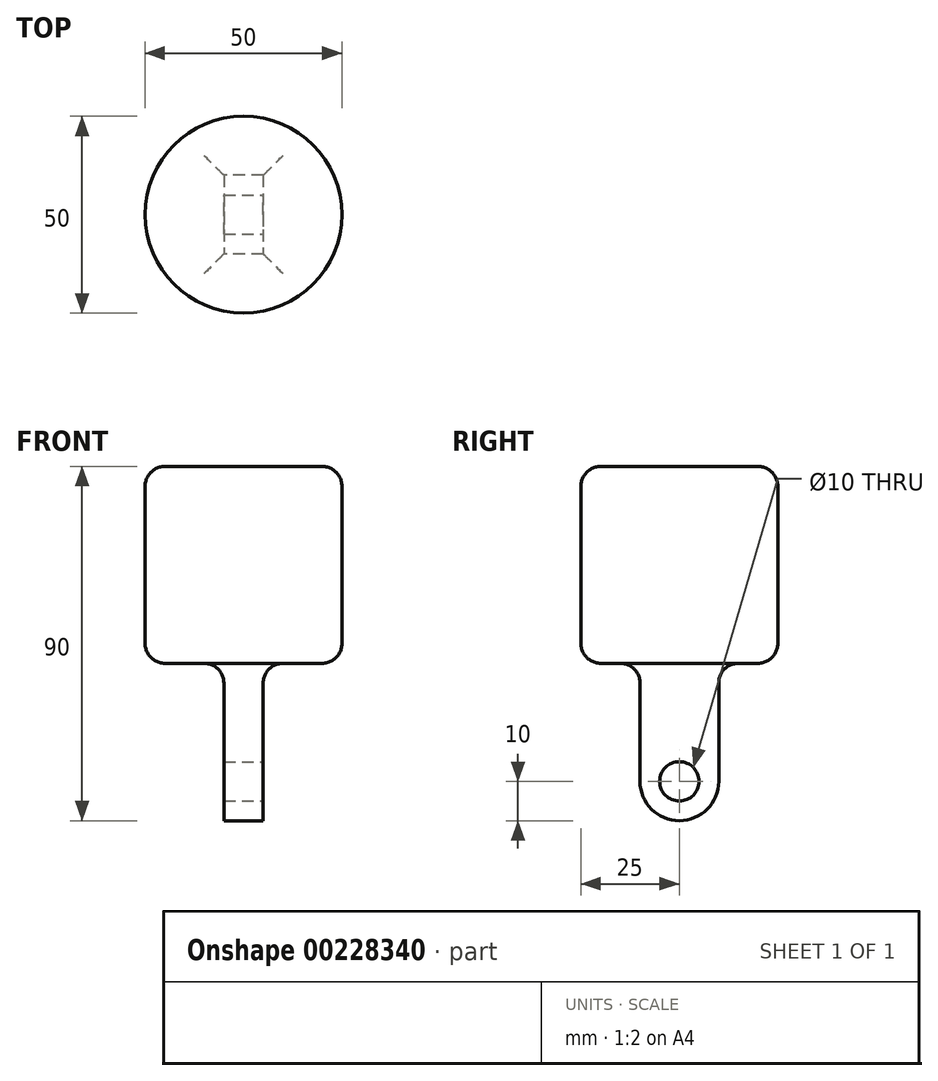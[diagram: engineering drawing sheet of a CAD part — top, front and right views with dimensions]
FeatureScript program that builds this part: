
annotation { "Feature Type Name" : "Feature", "Feature Type Description" : "" }
export const myFeature = defineFeature(function(context is Context, id is Id, definition is map)
    precondition{}
    {
        {
            var Q0;
            Q0=qCreatedBy(makeId("Top.planeOp"),FACE);
            var sketch = newSketch(context, id + "F0", { "sketchPlane" : qUnion([Q0])});
            skCircle(sketch, "E0", {"center": v(0, 0) * mm, "radius": 25 * mm});
            skSolve(sketch);
        }
        {
            var Q0;
            Q0=makeQuery(id+"F0.imprint","IMPRINT",FACE,{"disambiguationData":[TD([[makeQuery(id+"F0.imprint","IMPRINT",EDGE,{"derivedFrom":sQuery(id+"F0.wireOp",EDGE,"E0")}),1.0]])]});
            extrude(context, id + "F1", {"entities" : qUnion([Q0]), "depth" : 50 * mm});
        }
        {
            var Q0;
            Q0=makeQuery(id+"F1.opExtrude","CAP_FACE",FACE,{"disambiguationData":[OSD([sQuery(id+"F0.wireOp",EDGE,"E0")])],"isStart":true});
            var sketch = newSketch(context, id + "F2", { "sketchPlane" : qUnion([Q0])});
            skLineSegment(sketch, "E1.bottom", {"start": v(5, -10) * mm, "end": v(-5, -10) * mm});
            skLineSegment(sketch, "E1.top", {"start": v(5, 10) * mm, "end": v(-5, 10) * mm});
            skLineSegment(sketch, "E1.left", {"start": v(5, -10) * mm, "end": v(5, 10) * mm});
            skLineSegment(sketch, "E1.right", {"start": v(-5, -10) * mm, "end": v(-5, 10) * mm});
            skPoint(sketch, "E1.middle", {"position": v(0, 0) * mm});
            skSolve(sketch);
        }
        {
            var Q0;
            Q0=makeQuery(id+"F2.imprint","IMPRINT",FACE,{"disambiguationData":[TD([[makeQuery(id+"F2.imprint","IMPRINT",EDGE,{"derivedFrom":sQuery(id+"F2.wireOp",EDGE,"E1.bottom")}),-1.0]])]});
            extrude(context, id + "F3", {"entities" : qUnion([Q0]), "operationType" : NewBodyOperationType.ADD, "depth" : 40 * mm});
        }
        {
            var Q0;
            Q0=makeQuery(id+"F3.opExtrude","CAP_EDGE",EDGE,{"disambiguationData":[OSD([sQuery(id+"F2.wireOp",EDGE,"E1.bottom")])],"isStart":false});
            var Q1;
            Q1=makeQuery(id+"F3.opExtrude","CAP_EDGE",EDGE,{"disambiguationData":[OSD([sQuery(id+"F2.wireOp",EDGE,"E1.top")])],"isStart":false});
            fillet(context, id + "F6", {"entities" : qUnion([Q0, Q1]), "radius" : 10 * mm, "tangentPropagation" : true, "allowEdgeOverflow" : false});
        }
        {
            var Q0;
            Q0=makeQuery(id+"F1.opExtrude","CAP_EDGE",EDGE,{"disambiguationData":[OSD([sQuery(id+"F0.wireOp",EDGE,"E0")])],"isStart":false});
            var Q1;
            Q1=makeQuery(id+"F1.opExtrude","CAP_FACE",FACE,{"disambiguationData":[OSD([sQuery(id+"F0.wireOp",EDGE,"E0")])],"isStart":true});
            fillet(context, id + "F7", {"entities" : qUnion([Q0, Q1]), "radius" : 5 * mm, "tangentPropagation" : true, "allowEdgeOverflow" : false});
        }
        {
            var Q0;
            Q0=makeQuery(id+"F3.opExtrude","SWEPT_FACE",FACE,{"disambiguationData":[OSD([sQuery(id+"F2.wireOp",EDGE,"E1.right")])]});
            var sketch = newSketch(context, id + "F4", { "sketchPlane" : qUnion([Q0])});
            skPoint(sketch, "E2", {"position": v(0, -30) * mm});
            skSolve(sketch);
        }
        {
            var Q0;
            Q0=sQuery(id+"F4.wireOp",VERTEX,"E2");
            var Q1;
            Q1=makeQuery(id+"F1.opExtrude","SWEPT_BODY",BODY,{"disambiguationData":[OSD([sQuery(id+"F0.wireOp",EDGE,"E0")])]});
            hole(context, id + "F5", {"style" : HoleStyle.SIMPLE, "endStyle" : HoleEndStyle.THROUGH, "holeDiameter" : 10 * mm, "locations" : qUnion([Q0]), "scope" : qUnion([Q1]), "isTappedThrough" : true, "startStyle" : HoleStartStyle.PART});
        }
    });
